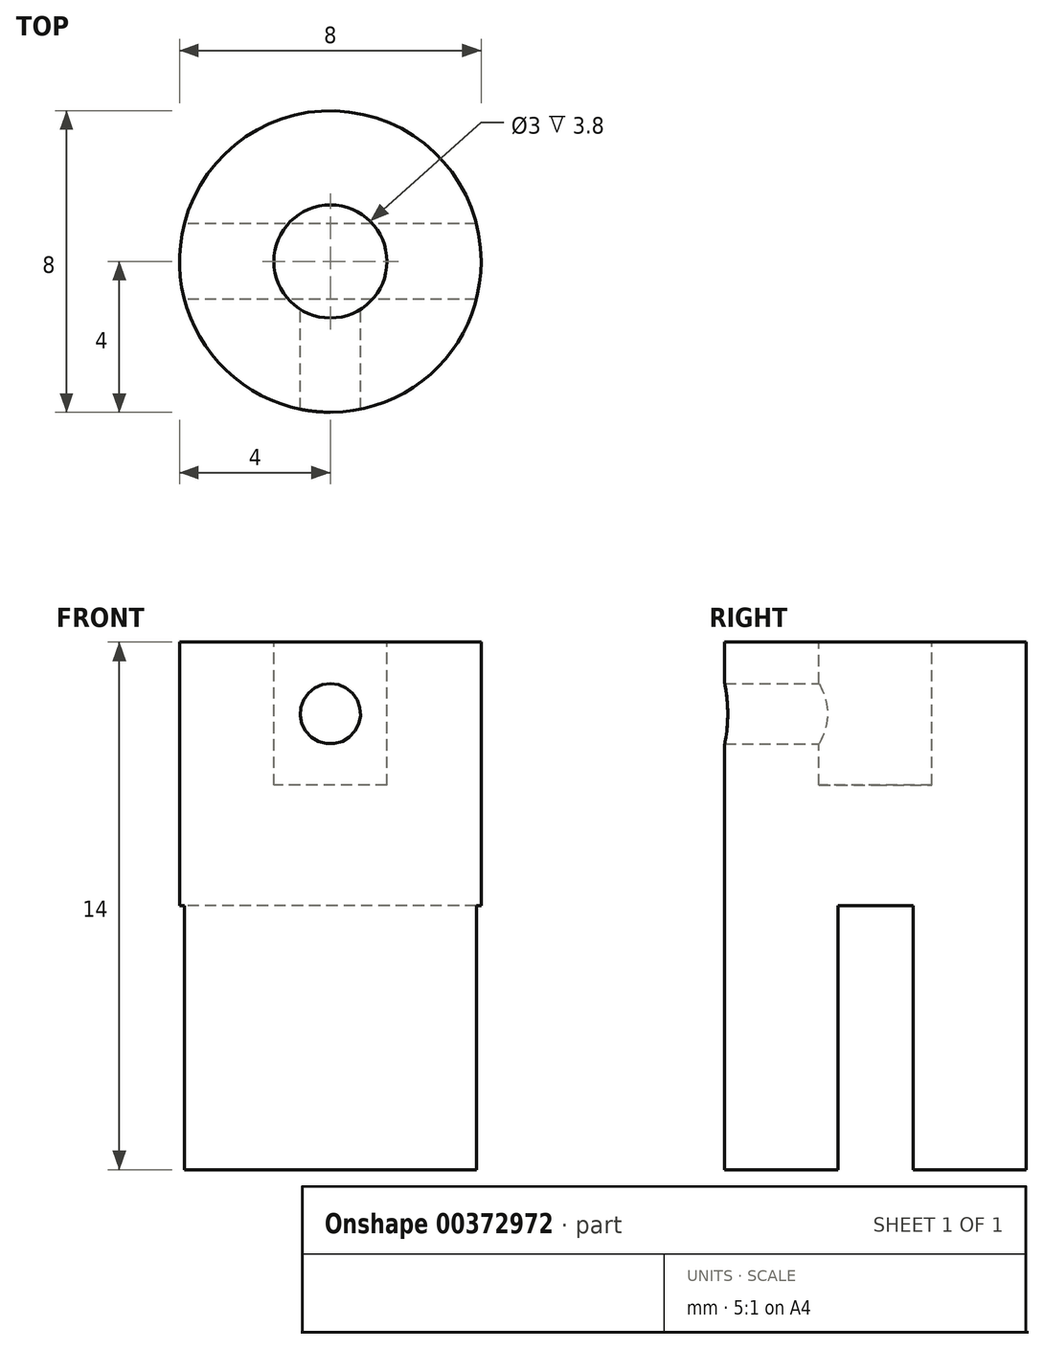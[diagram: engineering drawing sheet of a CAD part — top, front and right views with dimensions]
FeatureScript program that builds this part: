
annotation { "Feature Type Name" : "Feature", "Feature Type Description" : "" }
export const myFeature = defineFeature(function(context is Context, id is Id, definition is map)
    precondition{}
    {
        {
            var Q0;
            Q0=qCreatedBy(makeId("Top.planeOp"),FACE);
            var sketch = newSketch(context, id + "F0", { "sketchPlane" : qUnion([Q0])});
            skCircle(sketch, "E0", {"center": v(0, 0) * mm, "radius": 4 * mm});
            skSolve(sketch);
        }
        {
            var Q0;
            Q0 = qSketchRegion(id + "F0", true);
            extrude(context, id + "F1", {"entities" : qUnion([Q0]), "depth" : 14 * mm, "symmetric" : true});
        }
        {
            var Q0;
            Q0=makeQuery(id+"F1.opExtrude","CAP_FACE",FACE,{"disambiguationData":[OSD([sQuery(id+"F0.wireOp",EDGE,"E0")])],"isStart":false});
            var sketch = newSketch(context, id + "F2", { "sketchPlane" : qUnion([Q0])});
            skCircle(sketch, "E1", {"center": v(0, 0) * mm, "radius": 1.5 * mm});
            skSolve(sketch);
        }
        {
            var Q0;
            Q0 = qSketchRegion(id + "F2", true);
            extrude(context, id + "F3", {"entities" : qUnion([Q0]), "operationType" : NewBodyOperationType.REMOVE, "oppositeDirection" : true, "depth" : 3.8 * mm});
        }
        {
            var Q0;
            Q0=makeQuery(id+"F1.opExtrude","CAP_FACE",FACE,{"disambiguationData":[OSD([sQuery(id+"F0.wireOp",EDGE,"E0")])],"isStart":true});
            var sketch = newSketch(context, id + "F4", { "sketchPlane" : qUnion([Q0])});
            skLineSegment(sketch, "E2.bottom", {"start": v(5, 1) * mm, "end": v(-5, 1) * mm});
            skLineSegment(sketch, "E2.top", {"start": v(5, -1) * mm, "end": v(-5, -1) * mm});
            skLineSegment(sketch, "E2.left", {"start": v(5, 1) * mm, "end": v(5, -1) * mm});
            skLineSegment(sketch, "E2.right", {"start": v(-5, 1) * mm, "end": v(-5, -1) * mm});
            skPoint(sketch, "E2.middle", {"position": v(0, 0) * mm});
            skSolve(sketch);
        }
        {
            var Q0;
            Q0 = qSketchRegion(id + "F4", true);
            extrude(context, id + "F5", {"entities" : qUnion([Q0]), "operationType" : NewBodyOperationType.REMOVE, "oppositeDirection" : true, "depth" : 7 * mm});
        }
        {
            var Q0;
            Q0=qCreatedBy(makeId("Front.planeOp"),FACE);
            var sketch = newSketch(context, id + "F6", { "sketchPlane" : qUnion([Q0])});
            skCircle(sketch, "E3", {"center": v(0, 5.1) * mm, "radius": 0.8 * mm});
            skSolve(sketch);
        }
        {
            var Q0;
            Q0 = qSketchRegion(id + "F6", true);
            extrude(context, id + "F7", {"entities" : qUnion([Q0]), "operationType" : NewBodyOperationType.REMOVE, "endBound" : BoundingType.THROUGH_ALL, "depth" : 25 * mm});
        }
    });
